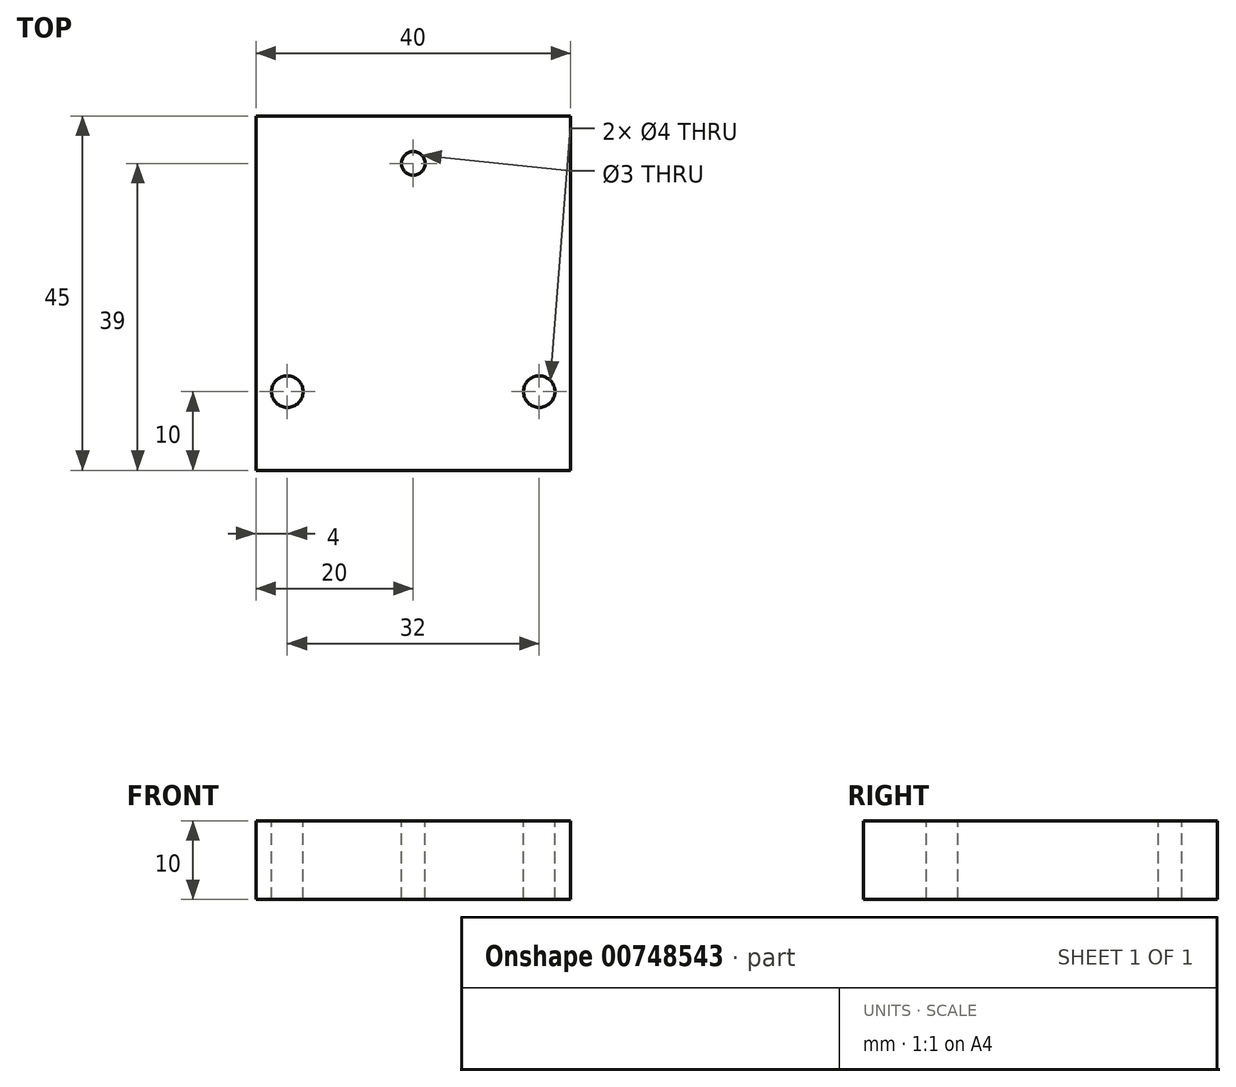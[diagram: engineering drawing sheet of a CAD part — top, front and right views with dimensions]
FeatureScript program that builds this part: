
annotation { "Feature Type Name" : "Feature", "Feature Type Description" : "" }
export const myFeature = defineFeature(function(context is Context, id is Id, definition is map)
    precondition{}
    {
        {
            var Q0;
            Q0=qCreatedBy(makeId("Top.planeOp"),FACE);
            var sketch = newSketch(context, id + "F0", { "sketchPlane" : qUnion([Q0])});
            skLineSegment(sketch, "E0.bottom", {"start": v(-20, 22.5) * mm, "end": v(20, 22.5) * mm});
            skLineSegment(sketch, "E0.top", {"start": v(-20, -22.5) * mm, "end": v(20, -22.5) * mm});
            skLineSegment(sketch, "E0.left", {"start": v(-20, 22.5) * mm, "end": v(-20, -22.5) * mm});
            skLineSegment(sketch, "E0.right", {"start": v(20, 22.5) * mm, "end": v(20, -22.5) * mm});
            skPoint(sketch, "E0.middle", {"position": v(0, 0) * mm});
            skSolve(sketch);
        }
        {
            var Q0;
            Q0=makeQuery(id+"F0.imprint","IMPRINT",FACE,{"disambiguationData":[TD([[makeQuery(id+"F0.imprint","IMPRINT",EDGE,{"derivedFrom":sQuery(id+"F0.wireOp",EDGE,"E0.bottom")}),-1.0]])]});
            extrude(context, id + "F1", {"entities" : qUnion([Q0]), "depth" : 10 * mm, "offsetDistance" : 25 * mm});
        }
        {
            var Q0;
            Q0=makeQuery(id+"F1.opExtrude","CAP_FACE",FACE,{"disambiguationData":[OSD([sQuery(id+"F0.wireOp",EDGE,"E0.bottom"),sQuery(id+"F0.wireOp",EDGE,"E0.top"),sQuery(id+"F0.wireOp",EDGE,"E0.left"),sQuery(id+"F0.wireOp",EDGE,"E0.right")])],"isStart":false});
            var sketch = newSketch(context, id + "F2", { "sketchPlane" : qUnion([Q0])});
            skCircle(sketch, "E1", {"center": v(0, 16.5) * mm, "radius": 1.5 * mm});
            skSolve(sketch);
        }
        {
            var Q0;
            Q0 = qSketchRegion(id + "F2", true);
            extrude(context, id + "F3", {"entities" : qUnion([Q0]), "operationType" : NewBodyOperationType.REMOVE, "oppositeDirection" : true, "depth" : 25 * mm, "offsetDistance" : 25 * mm});
        }
        {
            var Q0;
            Q0=makeQuery(id+"F1.opExtrude","CAP_FACE",FACE,{"disambiguationData":[OSD([sQuery(id+"F0.wireOp",EDGE,"E0.bottom"),sQuery(id+"F0.wireOp",EDGE,"E0.top"),sQuery(id+"F0.wireOp",EDGE,"E0.left"),sQuery(id+"F0.wireOp",EDGE,"E0.right")])],"isStart":false});
            var sketch = newSketch(context, id + "F4", { "sketchPlane" : qUnion([Q0])});
            skCircle(sketch, "E2", {"center": v(16, -12.5) * mm, "radius": 2 * mm});
            skCircle(sketch, "E3", {"center": v(-16, -12.5) * mm, "radius": 2 * mm});
            skSolve(sketch);
        }
        {
            var Q0;
            Q0 = qSketchRegion(id + "F4", true);
            extrude(context, id + "F5", {"entities" : qUnion([Q0]), "operationType" : NewBodyOperationType.REMOVE, "oppositeDirection" : true, "depth" : 25 * mm, "offsetDistance" : 25 * mm});
        }
    });
